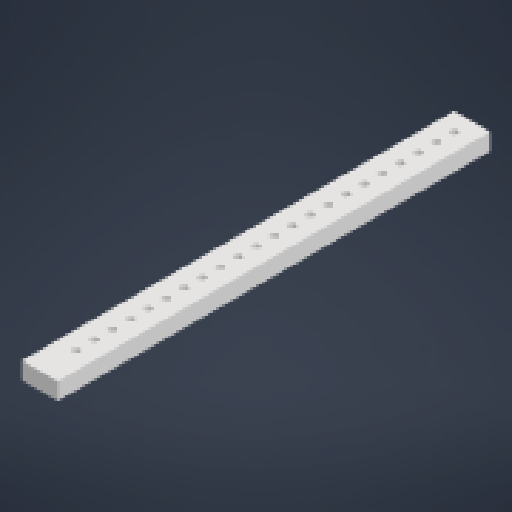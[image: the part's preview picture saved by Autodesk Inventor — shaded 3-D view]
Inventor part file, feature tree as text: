
AUTODESK INVENTOR PART (.ipt)
format: ipt  version: 2023 (Build 270158000, 158)  size: 159,744 bytes
history: native  units: in
note: dims shown in document units (in); Inventor stores cm internally (conversion verified against a paired STEP export)
features: extrude x1, sketch x1
ambient origin geometry x8: Origin, YZ Plane, XZ Plane, XY Plane, X Axis, Y Axis, Z Axis, Center Point
bodies: Body1 (feature_tree)
feature tree (2):
  extrude  "Extrusion2"  Depth=12.0in
  sketch  "Sketch1"  dims[d0=1.0in d1=12.0in d2=1.0in d3=90.0deg d4=0.1875in d14=8.6614in d16=0.5in d17=0.3937in d19=1.0in d21=0.47in d22=0.0in]
